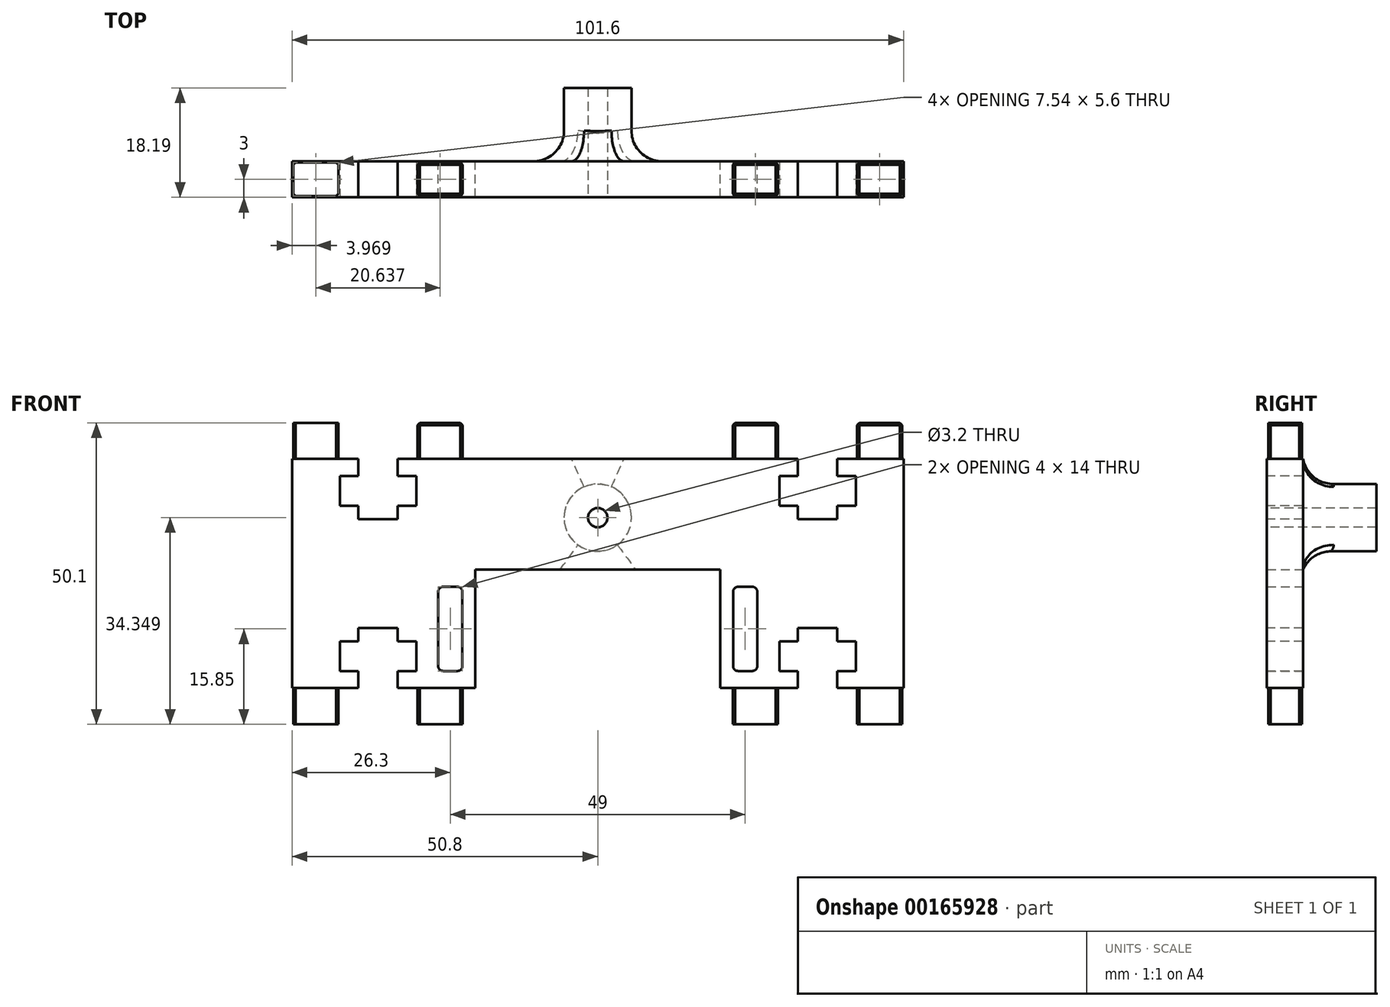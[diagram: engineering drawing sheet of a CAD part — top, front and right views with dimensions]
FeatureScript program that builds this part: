
annotation { "Feature Type Name" : "Feature", "Feature Type Description" : "" }
export const myFeature = defineFeature(function(context is Context, id is Id, definition is map)
    precondition{}
    {
        {
            var Q0;
            Q0=qCreatedBy(makeId("Front.planeOp"),FACE);
            var sketch = newSketch(context, id + "F0", { "sketchPlane" : qUnion([Q0])});
            skLineSegment(sketch, "E0.bottom", {"start": v(-50.8, 38.1) * mm, "end": v(50.8, 38.1) * mm});
            skLineSegment(sketch, "E0.top", {"start": v(-50.8, 0) * mm, "end": v(50.8, 0) * mm});
            skLineSegment(sketch, "E0.left", {"start": v(-50.8, 38.1) * mm, "end": v(-50.8, 0) * mm});
            skLineSegment(sketch, "E0.right", {"start": v(50.8, 38.1) * mm, "end": v(50.8, 0) * mm});
            skPoint(sketch, "E1", {"position": v(0, 0) * mm});
            skLineSegment(sketch, "E2.bottom", {"start": v(-20.35, 0) * mm, "end": v(20.35, 0) * mm});
            skLineSegment(sketch, "E2.top", {"start": v(-20.35, 19.7) * mm, "end": v(20.35, 19.7) * mm});
            skLineSegment(sketch, "E2.left", {"start": v(-20.35, 0) * mm, "end": v(-20.35, 19.7) * mm});
            skLineSegment(sketch, "E2.right", {"start": v(20.35, 0) * mm, "end": v(20.35, 19.7) * mm});
            skPoint(sketch, "E3", {"position": v(0, 19.7) * mm});
            skLineSegment(sketch, "E4.bottom", {"start": v(22.5, 16.85) * mm, "end": v(26.5, 16.85) * mm});
            skLineSegment(sketch, "E4.top", {"start": v(22.5, 2.85) * mm, "end": v(26.5, 2.85) * mm});
            skLineSegment(sketch, "E4.left", {"start": v(22.5, 16.85) * mm, "end": v(22.5, 2.85) * mm});
            skLineSegment(sketch, "E4.right", {"start": v(26.5, 16.85) * mm, "end": v(26.5, 2.85) * mm});
            skLineSegment(sketch, "E5", {"start": v(-20.35, 9.85) * mm, "end": v(36.92, 9.85) * mm, "construction": true});
            skPoint(sketch, "E6", {"position": v(26.5, 9.85) * mm});
            skLineSegment(sketch, "E7", {"start": v(24.5, 16.85) * mm, "end": v(24.5, 2.85) * mm, "construction": true});
            skLineSegment(sketch, "E8.MirrorCS", {"start": v(-22.5, 16.85) * mm, "end": v(-22.5, 2.85) * mm});
            skLineSegment(sketch, "E9.MirrorCS", {"start": v(-26.5, 16.85) * mm, "end": v(-26.5, 2.85) * mm});
            skLineSegment(sketch, "E10.MirrorCS", {"start": v(-22.5, 16.85) * mm, "end": v(-26.5, 16.85) * mm});
            skLineSegment(sketch, "E11.MirrorCS", {"start": v(-22.5, 2.85) * mm, "end": v(-26.5, 2.85) * mm});
            skSolve(sketch);
        }
        {
            var Q0;
            Q0=makeQuery(id+"F0.imprint","IMPRINT",FACE,{"disambiguationData":[TD([[makeQuery(id+"F0.imprint","IMPRINT",EDGE,{"derivedFrom":sQuery(id+"F0.wireOp",EDGE,"E0.bottom")}),-1.0]])]});
            extrude(context, id + "F1", {"entities" : qUnion([Q0]), "depth" : 6 * mm});
        }
        {
            var Q0;
            Q0=makeQuery(id+"F1.opExtrude","SWEPT_EDGE",EDGE,{"disambiguationData":[OSD([sQuery(id+"F0.wireOp",EDGE,"E9.MirrorCS"),sQuery(id+"F0.wireOp",EDGE,"E10.MirrorCS")])]});
            var Q1;
            Q1=makeQuery(id+"F1.opExtrude","SWEPT_EDGE",EDGE,{"disambiguationData":[OSD([sQuery(id+"F0.wireOp",EDGE,"E8.MirrorCS"),sQuery(id+"F0.wireOp",EDGE,"E11.MirrorCS")])]});
            var Q2;
            Q2=makeQuery(id+"F1.opExtrude","SWEPT_EDGE",EDGE,{"disambiguationData":[OSD([sQuery(id+"F0.wireOp",EDGE,"E8.MirrorCS"),sQuery(id+"F0.wireOp",EDGE,"E10.MirrorCS")])]});
            var Q3;
            Q3=makeQuery(id+"F1.opExtrude","SWEPT_EDGE",EDGE,{"disambiguationData":[OSD([sQuery(id+"F0.wireOp",EDGE,"E9.MirrorCS"),sQuery(id+"F0.wireOp",EDGE,"E11.MirrorCS")])]});
            var Q4;
            Q4=makeQuery(id+"F1.opExtrude","SWEPT_EDGE",EDGE,{"disambiguationData":[OSD([sQuery(id+"F0.wireOp",EDGE,"E4.top"),sQuery(id+"F0.wireOp",EDGE,"E4.left")])]});
            var Q5;
            Q5=makeQuery(id+"F1.opExtrude","SWEPT_EDGE",EDGE,{"disambiguationData":[OSD([sQuery(id+"F0.wireOp",EDGE,"E4.bottom"),sQuery(id+"F0.wireOp",EDGE,"E4.left")])]});
            var Q6;
            Q6=makeQuery(id+"F1.opExtrude","SWEPT_EDGE",EDGE,{"disambiguationData":[OSD([sQuery(id+"F0.wireOp",EDGE,"E4.bottom"),sQuery(id+"F0.wireOp",EDGE,"E4.right")])]});
            var Q7;
            Q7=makeQuery(id+"F1.opExtrude","SWEPT_EDGE",EDGE,{"disambiguationData":[OSD([sQuery(id+"F0.wireOp",EDGE,"E4.top"),sQuery(id+"F0.wireOp",EDGE,"E4.right")])]});
            fillet(context, id + "F2", {"entities" : qUnion([Q0, Q1, Q2, Q3, Q4, Q5, Q6, Q7]), "radius" : .8 * mm, "tangentPropagation" : true, "allowEdgeOverflow" : false});
        }
        {
            var Q0;
            {var subQ0=sQuery(id+"F0.wireOp",EDGE,"E0.top");Q0=makeQuery(id+"F1.opExtrude","SWEPT_FACE",FACE,{"disambiguationData":[OSD([subQ0]),TDD([makeQuery(id+"F0.imprint","IMPRINT",EDGE,{"disambiguationData":[TD([[makeQuery(id+"F0.imprint","INTERSECT",VERTEX,{"derivedFrom":[subQ0,sQuery(id+"F0.wireOp",EDGE,"E0.left")]}),-1.0]])],"derivedFrom":subQ0})])]});}
            var sketch = newSketch(context, id + "F3", { "sketchPlane" : qUnion([Q0])});
            skLineSegment(sketch, "E12.bottom", {"start": v(-50.8, 6) * mm, "end": v(-42.86, 6) * mm});
            skLineSegment(sketch, "E12.top", {"start": v(-50.8, 0) * mm, "end": v(-42.86, 0) * mm});
            skLineSegment(sketch, "E12.left", {"start": v(-50.8, 6) * mm, "end": v(-50.8, 0) * mm});
            skLineSegment(sketch, "E12.right", {"start": v(-42.86, 6) * mm, "end": v(-42.86, 0) * mm});
            skLineSegment(sketch, "E13.MirrorCS", {"start": v(50.8, 0) * mm, "end": v(42.86, 0) * mm});
            skLineSegment(sketch, "E14.MirrorCS", {"start": v(42.86, 6) * mm, "end": v(42.86, 0) * mm});
            skLineSegment(sketch, "E15.MirrorCS", {"start": v(50.8, 6) * mm, "end": v(42.86, 6) * mm});
            skLineSegment(sketch, "E16.MirrorCS", {"start": v(50.8, 6) * mm, "end": v(50.8, 0) * mm});
            skLineSegment(sketch, "E17.bottom", {"start": v(-30.16, 6) * mm, "end": v(-22.23, 6) * mm});
            skLineSegment(sketch, "E17.top", {"start": v(-30.16, 0) * mm, "end": v(-22.23, 0) * mm});
            skLineSegment(sketch, "E17.left", {"start": v(-30.16, 6) * mm, "end": v(-30.16, 0) * mm});
            skLineSegment(sketch, "E17.right", {"start": v(-22.23, 6) * mm, "end": v(-22.23, 0) * mm});
            skLineSegment(sketch, "E18.bottom", {"start": v(30.16, 6) * mm, "end": v(22.23, 6) * mm});
            skLineSegment(sketch, "E18.top", {"start": v(30.16, 0) * mm, "end": v(22.23, 0) * mm});
            skLineSegment(sketch, "E18.left", {"start": v(30.16, 6) * mm, "end": v(30.16, 0) * mm});
            skLineSegment(sketch, "E18.right", {"start": v(22.23, 6) * mm, "end": v(22.23, 0) * mm});
            skSolve(sketch);
        }
        {
            var Q0;
            Q0 = qSketchRegion(id + "F3", true);
            extrude(context, id + "F4", {"entities" : qUnion([Q0]), "operationType" : NewBodyOperationType.ADD, "depth" : 6 * mm});
        }
        {
            var Q0;
            Q0=makeQuery(id+"F1.opExtrude","SWEPT_FACE",FACE,{"disambiguationData":[OSD([sQuery(id+"F0.wireOp",EDGE,"E0.bottom")])]});
            var sketch = newSketch(context, id + "F5", { "sketchPlane" : qUnion([Q0])});
            skLineSegment(sketch, "E19.bottom", {"start": v(-50.8, 0) * mm, "end": v(-42.86, 0) * mm});
            skLineSegment(sketch, "E19.top", {"start": v(-50.8, -6) * mm, "end": v(-42.86, -6) * mm});
            skLineSegment(sketch, "E19.left", {"start": v(-50.8, 0) * mm, "end": v(-50.8, -6) * mm});
            skLineSegment(sketch, "E19.right", {"start": v(-42.86, 0) * mm, "end": v(-42.86, -6) * mm});
            skLineSegment(sketch, "E20.bottom", {"start": v(-30.16, 0) * mm, "end": v(-22.22, 0) * mm});
            skLineSegment(sketch, "E20.top", {"start": v(-30.16, -6) * mm, "end": v(-22.22, -6) * mm});
            skLineSegment(sketch, "E20.left", {"start": v(-30.16, 0) * mm, "end": v(-30.16, -6) * mm});
            skLineSegment(sketch, "E20.right", {"start": v(-22.22, 0) * mm, "end": v(-22.22, -6) * mm});
            skLineSegment(sketch, "E21.bottom", {"start": v(22.23, 0) * mm, "end": v(30.16, 0) * mm});
            skLineSegment(sketch, "E21.top", {"start": v(22.23, -6) * mm, "end": v(30.16, -6) * mm});
            skLineSegment(sketch, "E21.left", {"start": v(22.23, 0) * mm, "end": v(22.23, -6) * mm});
            skLineSegment(sketch, "E21.right", {"start": v(30.16, 0) * mm, "end": v(30.16, -6) * mm});
            skLineSegment(sketch, "E22.bottom", {"start": v(42.86, 0) * mm, "end": v(50.8, 0) * mm});
            skLineSegment(sketch, "E22.top", {"start": v(42.86, -6) * mm, "end": v(50.8, -6) * mm});
            skLineSegment(sketch, "E22.left", {"start": v(42.86, 0) * mm, "end": v(42.86, -6) * mm});
            skLineSegment(sketch, "E22.right", {"start": v(50.8, 0) * mm, "end": v(50.8, -6) * mm});
            skSolve(sketch);
        }
        {
            var Q0;
            Q0 = qSketchRegion(id + "F5", true);
            extrude(context, id + "F6", {"entities" : qUnion([Q0]), "operationType" : NewBodyOperationType.ADD, "depth" : 6 * mm});
        }
        {
            var Q0;
            Q0=makeQuery(id+"F6.boolean.opBoolean","MERGE",FACE,{"derivedFrom":[makeQuery(id+"F4.boolean.opBoolean","MERGE",FACE,{"derivedFrom":[makeQuery(id+"F1.opExtrude","CAP_FACE",FACE,{"disambiguationData":[OSD([sQuery(id+"F0.wireOp",EDGE,"E0.bottom"),sQuery(id+"F0.wireOp",EDGE,"E0.top"),sQuery(id+"F0.wireOp",EDGE,"E0.left"),sQuery(id+"F0.wireOp",EDGE,"E0.right"),sQuery(id+"F0.wireOp",EDGE,"E2.top"),sQuery(id+"F0.wireOp",EDGE,"E2.left"),sQuery(id+"F0.wireOp",EDGE,"E2.right"),sQuery(id+"F0.wireOp",EDGE,"E4.bottom"),sQuery(id+"F0.wireOp",EDGE,"E4.top"),sQuery(id+"F0.wireOp",EDGE,"E4.left"),sQuery(id+"F0.wireOp",EDGE,"E4.right"),sQuery(id+"F0.wireOp",EDGE,"E8.MirrorCS"),sQuery(id+"F0.wireOp",EDGE,"E9.MirrorCS"),sQuery(id+"F0.wireOp",EDGE,"E10.MirrorCS"),sQuery(id+"F0.wireOp",EDGE,"E11.MirrorCS")])],"isStart":false}),makeQuery(id+"F4.opExtrude","SWEPT_FACE",FACE,{"disambiguationData":[OSD([sQuery(id+"F3.wireOp",EDGE,"E12.bottom")])]}),makeQuery(id+"F4.opExtrude","SWEPT_FACE",FACE,{"disambiguationData":[OSD([sQuery(id+"F3.wireOp",EDGE,"E15.MirrorCS")])]}),makeQuery(id+"F4.opExtrude","SWEPT_FACE",FACE,{"disambiguationData":[OSD([sQuery(id+"F3.wireOp",EDGE,"E17.bottom")])]}),makeQuery(id+"F4.opExtrude","SWEPT_FACE",FACE,{"disambiguationData":[OSD([sQuery(id+"F3.wireOp",EDGE,"E18.bottom")])]})]}),makeQuery(id+"F6.opExtrude","SWEPT_FACE",FACE,{"disambiguationData":[OSD([sQuery(id+"F5.wireOp",EDGE,"E19.top")])]}),makeQuery(id+"F6.opExtrude","SWEPT_FACE",FACE,{"disambiguationData":[OSD([sQuery(id+"F5.wireOp",EDGE,"E20.top")])]}),makeQuery(id+"F6.opExtrude","SWEPT_FACE",FACE,{"disambiguationData":[OSD([sQuery(id+"F5.wireOp",EDGE,"E21.top")])]}),makeQuery(id+"F6.opExtrude","SWEPT_FACE",FACE,{"disambiguationData":[OSD([sQuery(id+"F5.wireOp",EDGE,"E22.top")])]})]});
            var sketch = newSketch(context, id + "F7", { "sketchPlane" : qUnion([Q0])});
            skLineSegment(sketch, "E23", {"start": v(0, 38.1) * mm, "end": v(0, 19.7) * mm, "construction": true});
            skLineSegment(sketch, "E24", {"start": v(-50.8, 19.05) * mm, "end": v(50.8, 19.05) * mm, "construction": true});
            skLineSegment(sketch, "E25", {"start": v(-36.51, 38.1) * mm, "end": v(-39.76, 38.1) * mm});
            skLineSegment(sketch, "E26", {"start": v(-39.76, 38.1) * mm, "end": v(-39.76, 35.3) * mm});
            skLineSegment(sketch, "E27", {"start": v(-39.76, 35.3) * mm, "end": v(-42.86, 35.3) * mm});
            skLineSegment(sketch, "E28", {"start": v(-42.86, 35.3) * mm, "end": v(-42.86, 30.3) * mm});
            skLineSegment(sketch, "E29", {"start": v(-42.86, 30.3) * mm, "end": v(-39.76, 30.3) * mm});
            skLineSegment(sketch, "E30", {"start": v(-39.76, 30.3) * mm, "end": v(-39.76, 28.1) * mm});
            skLineSegment(sketch, "E31", {"start": v(-39.76, 28.1) * mm, "end": v(-36.51, 28.1) * mm});
            skLineSegment(sketch, "E32", {"start": v(-36.51, 38.1) * mm, "end": v(-36.51, 28.1) * mm, "construction": true});
            skLineSegment(sketch, "E33.MirrorCS", {"start": v(-36.51, 38.1) * mm, "end": v(-33.26, 38.1) * mm});
            skLineSegment(sketch, "E34.MirrorCS", {"start": v(-33.26, 38.1) * mm, "end": v(-33.26, 35.3) * mm});
            skLineSegment(sketch, "E35.MirrorCS", {"start": v(-33.26, 35.3) * mm, "end": v(-30.16, 35.3) * mm});
            skLineSegment(sketch, "E36.MirrorCS", {"start": v(-30.16, 35.3) * mm, "end": v(-30.16, 30.3) * mm});
            skLineSegment(sketch, "E37.MirrorCS", {"start": v(-30.16, 30.3) * mm, "end": v(-33.26, 30.3) * mm});
            skLineSegment(sketch, "E38.MirrorCS", {"start": v(-33.26, 30.3) * mm, "end": v(-33.26, 28.1) * mm});
            skLineSegment(sketch, "E39.MirrorCS", {"start": v(-33.26, 28.1) * mm, "end": v(-36.51, 28.1) * mm});
            skLineSegment(sketch, "E40.MirrorCS", {"start": v(39.76, 38.1) * mm, "end": v(39.76, 35.3) * mm});
            skLineSegment(sketch, "E41.MirrorCS", {"start": v(33.26, 38.1) * mm, "end": v(33.26, 35.3) * mm});
            skLineSegment(sketch, "E42.MirrorCS", {"start": v(33.26, 35.3) * mm, "end": v(30.16, 35.3) * mm});
            skLineSegment(sketch, "E43.MirrorCS", {"start": v(36.51, 38.1) * mm, "end": v(39.76, 38.1) * mm});
            skLineSegment(sketch, "E44.MirrorCS", {"start": v(36.51, 38.1) * mm, "end": v(33.26, 38.1) * mm});
            skLineSegment(sketch, "E45.MirrorCS", {"start": v(30.16, 35.3) * mm, "end": v(30.16, 30.3) * mm});
            skLineSegment(sketch, "E46.MirrorCS", {"start": v(30.16, 30.3) * mm, "end": v(33.26, 30.3) * mm});
            skLineSegment(sketch, "E47.MirrorCS", {"start": v(33.26, 30.3) * mm, "end": v(33.26, 28.1) * mm});
            skLineSegment(sketch, "E48.MirrorCS", {"start": v(33.26, 28.1) * mm, "end": v(36.51, 28.1) * mm});
            skLineSegment(sketch, "E49.MirrorCS", {"start": v(39.76, 28.1) * mm, "end": v(36.51, 28.1) * mm});
            skLineSegment(sketch, "E50.MirrorCS", {"start": v(39.76, 30.3) * mm, "end": v(39.76, 28.1) * mm});
            skLineSegment(sketch, "E51.MirrorCS", {"start": v(42.86, 30.3) * mm, "end": v(39.76, 30.3) * mm});
            skLineSegment(sketch, "E52.MirrorCS", {"start": v(42.86, 35.3) * mm, "end": v(42.86, 30.3) * mm});
            skLineSegment(sketch, "E53.MirrorCS", {"start": v(39.76, 35.3) * mm, "end": v(42.86, 35.3) * mm});
            skLineSegment(sketch, "E54.MirrorCS", {"start": v(33.26, 0) * mm, "end": v(33.26, 2.8) * mm});
            skLineSegment(sketch, "E55.MirrorCS", {"start": v(33.26, 2.8) * mm, "end": v(30.16, 2.8) * mm});
            skLineSegment(sketch, "E56.MirrorCS", {"start": v(30.16, 2.8) * mm, "end": v(30.16, 7.8) * mm});
            skLineSegment(sketch, "E57.MirrorCS", {"start": v(30.16, 7.8) * mm, "end": v(33.26, 7.8) * mm});
            skLineSegment(sketch, "E58.MirrorCS", {"start": v(33.26, 7.8) * mm, "end": v(33.26, 10) * mm});
            skLineSegment(sketch, "E59.MirrorCS", {"start": v(33.26, 10) * mm, "end": v(36.51, 10) * mm});
            skLineSegment(sketch, "E60.MirrorCS", {"start": v(39.76, 10) * mm, "end": v(36.51, 10) * mm});
            skLineSegment(sketch, "E61.MirrorCS", {"start": v(39.76, 7.8) * mm, "end": v(39.76, 10) * mm});
            skLineSegment(sketch, "E62.MirrorCS", {"start": v(42.86, 7.8) * mm, "end": v(39.76, 7.8) * mm});
            skLineSegment(sketch, "E63.MirrorCS", {"start": v(42.86, 2.8) * mm, "end": v(42.86, 7.8) * mm});
            skLineSegment(sketch, "E64.MirrorCS", {"start": v(39.76, 2.8) * mm, "end": v(42.86, 2.8) * mm});
            skLineSegment(sketch, "E65.MirrorCS", {"start": v(39.76, 0) * mm, "end": v(39.76, 2.8) * mm});
            skLineSegment(sketch, "E66.MirrorCS", {"start": v(36.51, 0) * mm, "end": v(39.76, 0) * mm});
            skLineSegment(sketch, "E67.MirrorCS", {"start": v(36.51, 0) * mm, "end": v(33.26, 0) * mm});
            skLineSegment(sketch, "E68.MirrorCS", {"start": v(-39.76, 0) * mm, "end": v(-39.76, 2.8) * mm});
            skLineSegment(sketch, "E69.MirrorCS", {"start": v(-36.51, 0) * mm, "end": v(-39.76, 0) * mm});
            skLineSegment(sketch, "E70.MirrorCS", {"start": v(-36.51, 0) * mm, "end": v(-33.26, 0) * mm});
            skLineSegment(sketch, "E71.MirrorCS", {"start": v(-33.26, 0) * mm, "end": v(-33.26, 2.8) * mm});
            skLineSegment(sketch, "E72.MirrorCS", {"start": v(-33.26, 2.8) * mm, "end": v(-30.16, 2.8) * mm});
            skLineSegment(sketch, "E73.MirrorCS", {"start": v(-30.16, 2.8) * mm, "end": v(-30.16, 7.8) * mm});
            skLineSegment(sketch, "E74.MirrorCS", {"start": v(-30.16, 7.8) * mm, "end": v(-33.26, 7.8) * mm});
            skLineSegment(sketch, "E75.MirrorCS", {"start": v(-33.26, 10) * mm, "end": v(-36.51, 10) * mm});
            skLineSegment(sketch, "E76.MirrorCS", {"start": v(-39.76, 10) * mm, "end": v(-36.51, 10) * mm});
            skLineSegment(sketch, "E77.MirrorCS", {"start": v(-39.76, 7.8) * mm, "end": v(-39.76, 10) * mm});
            skLineSegment(sketch, "E78.MirrorCS", {"start": v(-42.86, 7.8) * mm, "end": v(-39.76, 7.8) * mm});
            skLineSegment(sketch, "E79.MirrorCS", {"start": v(-42.86, 2.8) * mm, "end": v(-42.86, 7.8) * mm});
            skLineSegment(sketch, "E80.MirrorCS", {"start": v(-39.76, 2.8) * mm, "end": v(-42.86, 2.8) * mm});
            skLineSegment(sketch, "E81.MirrorCS", {"start": v(-33.26, 7.8) * mm, "end": v(-33.26, 10) * mm});
            skSolve(sketch);
        }
        {
            var Q0;
            Q0 = qSketchRegion(id + "F7", true);
            extrude(context, id + "F8", {"entities" : qUnion([Q0]), "operationType" : NewBodyOperationType.REMOVE, "oppositeDirection" : true, "depth" : 25.4 * mm});
        }
        {
            var Q0;
            Q0=makeQuery(id+"F4.opExtrude","CAP_FACE",FACE,{"disambiguationData":[OSD([sQuery(id+"F3.wireOp",EDGE,"E12.bottom"),sQuery(id+"F3.wireOp",EDGE,"E12.top"),sQuery(id+"F3.wireOp",EDGE,"E12.left"),sQuery(id+"F3.wireOp",EDGE,"E12.right")])],"isStart":false});
            var sketch = newSketch(context, id + "F9", { "sketchPlane" : qUnion([Q0])});
            skLineSegment(sketch, "E82.bottom", {"start": v(-50.6, 5.8) * mm, "end": v(-43.06, 5.8) * mm});
            skLineSegment(sketch, "E82.top", {"start": v(-50.6, 0.2) * mm, "end": v(-43.06, 0.2) * mm});
            skLineSegment(sketch, "E82.left", {"start": v(-50.6, 5.8) * mm, "end": v(-50.6, 0.2) * mm});
            skLineSegment(sketch, "E82.right", {"start": v(-43.06, 5.8) * mm, "end": v(-43.06, 0.2) * mm});
            skLineSegment(sketch, "E83.bottom", {"start": v(-50.8, 6) * mm, "end": v(-42.86, 6) * mm});
            skLineSegment(sketch, "E83.top", {"start": v(-50.8, 0) * mm, "end": v(-42.86, 0) * mm});
            skLineSegment(sketch, "E83.left", {"start": v(-50.8, 6) * mm, "end": v(-50.8, 0) * mm});
            skLineSegment(sketch, "E83.right", {"start": v(-42.86, 6) * mm, "end": v(-42.86, 0) * mm});
            skLineSegment(sketch, "E84.bottom", {"start": v(-30.16, 6) * mm, "end": v(-22.23, 6) * mm});
            skLineSegment(sketch, "E84.top", {"start": v(-30.16, 0) * mm, "end": v(-22.23, 0) * mm});
            skLineSegment(sketch, "E84.left", {"start": v(-30.16, 6) * mm, "end": v(-30.16, 0) * mm});
            skLineSegment(sketch, "E84.right", {"start": v(-22.23, 6) * mm, "end": v(-22.23, 0) * mm});
            skLineSegment(sketch, "E85.bottom", {"start": v(-29.96, 5.8) * mm, "end": v(-22.43, 5.8) * mm});
            skLineSegment(sketch, "E85.top", {"start": v(-29.96, 0.2) * mm, "end": v(-22.43, 0.2) * mm});
            skLineSegment(sketch, "E85.left", {"start": v(-29.96, 5.8) * mm, "end": v(-29.96, 0.2) * mm});
            skLineSegment(sketch, "E85.right", {"start": v(-22.43, 5.8) * mm, "end": v(-22.43, 0.2) * mm});
            skLineSegment(sketch, "E86", {"start": v(0, 7.46) * mm, "end": v(0, -0.5) * mm, "construction": true});
            skLineSegment(sketch, "E87.MirrorCS", {"start": v(22.23, 6) * mm, "end": v(22.23, 0) * mm});
            skLineSegment(sketch, "E88.MirrorCS", {"start": v(30.16, 0) * mm, "end": v(22.23, 0) * mm});
            skLineSegment(sketch, "E89.MirrorCS", {"start": v(30.16, 6) * mm, "end": v(30.16, 0) * mm});
            skLineSegment(sketch, "E90.MirrorCS", {"start": v(30.16, 6) * mm, "end": v(22.23, 6) * mm});
            skLineSegment(sketch, "E91.MirrorCS", {"start": v(29.96, 5.8) * mm, "end": v(22.43, 5.8) * mm});
            skLineSegment(sketch, "E92.MirrorCS", {"start": v(22.43, 5.8) * mm, "end": v(22.43, 0.2) * mm});
            skLineSegment(sketch, "E93.MirrorCS", {"start": v(29.96, 0.2) * mm, "end": v(22.43, 0.2) * mm});
            skLineSegment(sketch, "E94.MirrorCS", {"start": v(29.96, 5.8) * mm, "end": v(29.96, 0.2) * mm});
            skLineSegment(sketch, "E95.MirrorCS", {"start": v(50.6, 5.8) * mm, "end": v(50.6, 0.2) * mm});
            skLineSegment(sketch, "E96.MirrorCS", {"start": v(50.8, 6) * mm, "end": v(50.8, 0) * mm});
            skLineSegment(sketch, "E97.MirrorCS", {"start": v(50.8, 6) * mm, "end": v(42.86, 6) * mm});
            skLineSegment(sketch, "E98.MirrorCS", {"start": v(42.86, 6) * mm, "end": v(42.86, 0) * mm});
            skLineSegment(sketch, "E99.MirrorCS", {"start": v(50.8, 0) * mm, "end": v(42.86, 0) * mm});
            skLineSegment(sketch, "E100.MirrorCS", {"start": v(50.6, 0.2) * mm, "end": v(43.06, 0.2) * mm});
            skLineSegment(sketch, "E101.MirrorCS", {"start": v(43.06, 5.8) * mm, "end": v(43.06, 0.2) * mm});
            skLineSegment(sketch, "E102.MirrorCS", {"start": v(50.6, 5.8) * mm, "end": v(43.06, 5.8) * mm});
            skSolve(sketch);
        }
        {
            var Q0;
            Q0 = qSketchRegion(id + "F9", true);
            extrude(context, id + "F10", {"entities" : qUnion([Q0]), "operationType" : NewBodyOperationType.REMOVE, "oppositeDirection" : true, "depth" : 6 * mm});
        }
        {
            var Q0;
            Q0=makeQuery(id+"F10.boolean.opBoolean","COPY",EDGE,{"derivedFrom":makeQuery(id+"F10.opExtrude","SWEPT_EDGE",EDGE,{"disambiguationData":[OSD([sQuery(id+"F9.wireOp",EDGE,"E82.bottom"),sQuery(id+"F9.wireOp",EDGE,"E82.left")])]})});
            var Q1;
            Q1=makeQuery(id+"F10.boolean.opBoolean","COPY",EDGE,{"derivedFrom":makeQuery(id+"F10.opExtrude","SWEPT_EDGE",EDGE,{"disambiguationData":[OSD([sQuery(id+"F9.wireOp",EDGE,"E82.bottom"),sQuery(id+"F9.wireOp",EDGE,"E82.right")])]})});
            var Q2;
            Q2=makeQuery(id+"F10.boolean.opBoolean","COPY",EDGE,{"derivedFrom":makeQuery(id+"F10.opExtrude","CAP_EDGE",EDGE,{"disambiguationData":[OSD([sQuery(id+"F9.wireOp",EDGE,"E82.bottom")])],"isStart":true})});
            var Q3;
            Q3=makeQuery(id+"F10.boolean.opBoolean","COPY",EDGE,{"derivedFrom":makeQuery(id+"F10.opExtrude","CAP_EDGE",EDGE,{"disambiguationData":[OSD([sQuery(id+"F9.wireOp",EDGE,"E82.right")])],"isStart":true})});
            var Q4;
            Q4=makeQuery(id+"F10.boolean.opBoolean","COPY",EDGE,{"derivedFrom":makeQuery(id+"F10.opExtrude","CAP_EDGE",EDGE,{"disambiguationData":[OSD([sQuery(id+"F9.wireOp",EDGE,"E82.top")])],"isStart":true})});
            var Q5;
            Q5=makeQuery(id+"F10.boolean.opBoolean","COPY",EDGE,{"derivedFrom":makeQuery(id+"F10.opExtrude","CAP_EDGE",EDGE,{"disambiguationData":[OSD([sQuery(id+"F9.wireOp",EDGE,"E82.left")])],"isStart":true})});
            var Q6;
            Q6=makeQuery(id+"F10.boolean.opBoolean","COPY",EDGE,{"derivedFrom":makeQuery(id+"F10.opExtrude","SWEPT_EDGE",EDGE,{"disambiguationData":[OSD([sQuery(id+"F9.wireOp",EDGE,"E82.top"),sQuery(id+"F9.wireOp",EDGE,"E82.left")])]})});
            var Q7;
            Q7=makeQuery(id+"F10.boolean.opBoolean","COPY",EDGE,{"derivedFrom":makeQuery(id+"F10.opExtrude","SWEPT_EDGE",EDGE,{"disambiguationData":[OSD([sQuery(id+"F9.wireOp",EDGE,"E82.top"),sQuery(id+"F9.wireOp",EDGE,"E82.right")])]})});
            var Q8;
            Q8=makeQuery(id+"F10.boolean.opBoolean","COPY",EDGE,{"derivedFrom":makeQuery(id+"F10.opExtrude","SWEPT_EDGE",EDGE,{"disambiguationData":[OSD([sQuery(id+"F9.wireOp",EDGE,"E85.top"),sQuery(id+"F9.wireOp",EDGE,"E85.left")])]})});
            var Q9;
            Q9=makeQuery(id+"F10.boolean.opBoolean","COPY",EDGE,{"derivedFrom":makeQuery(id+"F10.opExtrude","SWEPT_EDGE",EDGE,{"disambiguationData":[OSD([sQuery(id+"F9.wireOp",EDGE,"E85.bottom"),sQuery(id+"F9.wireOp",EDGE,"E85.left")])]})});
            var Q10;
            Q10=makeQuery(id+"F10.boolean.opBoolean","COPY",EDGE,{"derivedFrom":makeQuery(id+"F10.opExtrude","SWEPT_EDGE",EDGE,{"disambiguationData":[OSD([sQuery(id+"F9.wireOp",EDGE,"E85.top"),sQuery(id+"F9.wireOp",EDGE,"E85.right")])]})});
            var Q11;
            Q11=makeQuery(id+"F10.boolean.opBoolean","COPY",EDGE,{"derivedFrom":makeQuery(id+"F10.opExtrude","CAP_EDGE",EDGE,{"disambiguationData":[OSD([sQuery(id+"F9.wireOp",EDGE,"E85.top")])],"isStart":true})});
            var Q12;
            Q12=makeQuery(id+"F10.boolean.opBoolean","COPY",EDGE,{"derivedFrom":makeQuery(id+"F10.opExtrude","CAP_EDGE",EDGE,{"disambiguationData":[OSD([sQuery(id+"F9.wireOp",EDGE,"E85.left")])],"isStart":true})});
            var Q13;
            Q13=makeQuery(id+"F10.boolean.opBoolean","COPY",EDGE,{"derivedFrom":makeQuery(id+"F10.opExtrude","CAP_EDGE",EDGE,{"disambiguationData":[OSD([sQuery(id+"F9.wireOp",EDGE,"E85.bottom")])],"isStart":true})});
            var Q14;
            Q14=makeQuery(id+"F10.boolean.opBoolean","COPY",EDGE,{"derivedFrom":makeQuery(id+"F10.opExtrude","CAP_EDGE",EDGE,{"disambiguationData":[OSD([sQuery(id+"F9.wireOp",EDGE,"E85.right")])],"isStart":true})});
            var Q15;
            Q15=makeQuery(id+"F10.boolean.opBoolean","COPY",EDGE,{"derivedFrom":makeQuery(id+"F10.opExtrude","SWEPT_EDGE",EDGE,{"disambiguationData":[OSD([sQuery(id+"F9.wireOp",EDGE,"E85.bottom"),sQuery(id+"F9.wireOp",EDGE,"E85.right")])]})});
            var Q16;
            Q16=makeQuery(id+"F10.boolean.opBoolean","COPY",EDGE,{"derivedFrom":makeQuery(id+"F10.opExtrude","SWEPT_EDGE",EDGE,{"disambiguationData":[OSD([sQuery(id+"F9.wireOp",EDGE,"E91.MirrorCS"),sQuery(id+"F9.wireOp",EDGE,"E92.MirrorCS")])]})});
            var Q17;
            Q17=makeQuery(id+"F10.boolean.opBoolean","COPY",EDGE,{"derivedFrom":makeQuery(id+"F10.opExtrude","SWEPT_EDGE",EDGE,{"disambiguationData":[OSD([sQuery(id+"F9.wireOp",EDGE,"E91.MirrorCS"),sQuery(id+"F9.wireOp",EDGE,"E94.MirrorCS")])]})});
            var Q18;
            Q18=makeQuery(id+"F10.boolean.opBoolean","COPY",EDGE,{"derivedFrom":makeQuery(id+"F10.opExtrude","CAP_EDGE",EDGE,{"disambiguationData":[OSD([sQuery(id+"F9.wireOp",EDGE,"E91.MirrorCS")])],"isStart":true})});
            var Q19;
            Q19=makeQuery(id+"F10.boolean.opBoolean","COPY",EDGE,{"derivedFrom":makeQuery(id+"F10.opExtrude","CAP_EDGE",EDGE,{"disambiguationData":[OSD([sQuery(id+"F9.wireOp",EDGE,"E94.MirrorCS")])],"isStart":true})});
            var Q20;
            Q20=makeQuery(id+"F10.boolean.opBoolean","COPY",EDGE,{"derivedFrom":makeQuery(id+"F10.opExtrude","CAP_EDGE",EDGE,{"disambiguationData":[OSD([sQuery(id+"F9.wireOp",EDGE,"E93.MirrorCS")])],"isStart":true})});
            var Q21;
            Q21=makeQuery(id+"F10.boolean.opBoolean","COPY",EDGE,{"derivedFrom":makeQuery(id+"F10.opExtrude","CAP_EDGE",EDGE,{"disambiguationData":[OSD([sQuery(id+"F9.wireOp",EDGE,"E92.MirrorCS")])],"isStart":true})});
            var Q22;
            Q22=makeQuery(id+"F10.boolean.opBoolean","COPY",EDGE,{"derivedFrom":makeQuery(id+"F10.opExtrude","SWEPT_EDGE",EDGE,{"disambiguationData":[OSD([sQuery(id+"F9.wireOp",EDGE,"E92.MirrorCS"),sQuery(id+"F9.wireOp",EDGE,"E93.MirrorCS")])]})});
            var Q23;
            Q23=makeQuery(id+"F10.boolean.opBoolean","COPY",EDGE,{"derivedFrom":makeQuery(id+"F10.opExtrude","SWEPT_EDGE",EDGE,{"disambiguationData":[OSD([sQuery(id+"F9.wireOp",EDGE,"E93.MirrorCS"),sQuery(id+"F9.wireOp",EDGE,"E94.MirrorCS")])]})});
            var Q24;
            Q24=makeQuery(id+"F10.boolean.opBoolean","COPY",EDGE,{"derivedFrom":makeQuery(id+"F10.opExtrude","SWEPT_EDGE",EDGE,{"disambiguationData":[OSD([sQuery(id+"F9.wireOp",EDGE,"E100.MirrorCS"),sQuery(id+"F9.wireOp",EDGE,"E101.MirrorCS")])]})});
            var Q25;
            Q25=makeQuery(id+"F10.boolean.opBoolean","COPY",EDGE,{"derivedFrom":makeQuery(id+"F10.opExtrude","SWEPT_EDGE",EDGE,{"disambiguationData":[OSD([sQuery(id+"F9.wireOp",EDGE,"E101.MirrorCS"),sQuery(id+"F9.wireOp",EDGE,"E102.MirrorCS")])]})});
            var Q26;
            Q26=makeQuery(id+"F10.boolean.opBoolean","COPY",EDGE,{"derivedFrom":makeQuery(id+"F10.opExtrude","SWEPT_EDGE",EDGE,{"disambiguationData":[OSD([sQuery(id+"F9.wireOp",EDGE,"E95.MirrorCS"),sQuery(id+"F9.wireOp",EDGE,"E100.MirrorCS")])]})});
            var Q27;
            Q27=makeQuery(id+"F10.boolean.opBoolean","COPY",EDGE,{"derivedFrom":makeQuery(id+"F10.opExtrude","CAP_EDGE",EDGE,{"disambiguationData":[OSD([sQuery(id+"F9.wireOp",EDGE,"E100.MirrorCS")])],"isStart":true})});
            var Q28;
            Q28=makeQuery(id+"F10.boolean.opBoolean","COPY",EDGE,{"derivedFrom":makeQuery(id+"F10.opExtrude","CAP_EDGE",EDGE,{"disambiguationData":[OSD([sQuery(id+"F9.wireOp",EDGE,"E101.MirrorCS")])],"isStart":true})});
            var Q29;
            Q29=makeQuery(id+"F10.boolean.opBoolean","COPY",EDGE,{"derivedFrom":makeQuery(id+"F10.opExtrude","CAP_EDGE",EDGE,{"disambiguationData":[OSD([sQuery(id+"F9.wireOp",EDGE,"E102.MirrorCS")])],"isStart":true})});
            var Q30;
            Q30=makeQuery(id+"F10.boolean.opBoolean","COPY",EDGE,{"derivedFrom":makeQuery(id+"F10.opExtrude","CAP_EDGE",EDGE,{"disambiguationData":[OSD([sQuery(id+"F9.wireOp",EDGE,"E95.MirrorCS")])],"isStart":true})});
            var Q31;
            Q31=makeQuery(id+"F10.boolean.opBoolean","COPY",EDGE,{"derivedFrom":makeQuery(id+"F10.opExtrude","SWEPT_EDGE",EDGE,{"disambiguationData":[OSD([sQuery(id+"F9.wireOp",EDGE,"E95.MirrorCS"),sQuery(id+"F9.wireOp",EDGE,"E102.MirrorCS")])]})});
            chamfer(context, id + "F11", {"entities" : qUnion([Q0, Q1, Q2, Q3, Q4, Q5, Q6, Q7, Q8, Q9, Q10, Q11, Q12, Q13, Q14, Q15, Q16, Q17, Q18, Q19, Q20, Q21, Q22, Q23, Q24, Q25, Q26, Q27, Q28, Q29, Q30, Q31]), "width" : .4 * mm, "tangentPropagation" : true});
        }
        {
            var Q0;
            Q0=makeQuery(id+"F6.opExtrude","CAP_FACE",FACE,{"disambiguationData":[OSD([sQuery(id+"F5.wireOp",EDGE,"E19.bottom"),sQuery(id+"F5.wireOp",EDGE,"E19.top"),sQuery(id+"F5.wireOp",EDGE,"E19.left"),sQuery(id+"F5.wireOp",EDGE,"E19.right")])],"isStart":false});
            var sketch = newSketch(context, id + "F12", { "sketchPlane" : qUnion([Q0])});
            skLineSegment(sketch, "E103.bottom", {"start": v(-50.6, -0.2) * mm, "end": v(-43.06, -0.2) * mm});
            skLineSegment(sketch, "E103.top", {"start": v(-50.6, -5.8) * mm, "end": v(-43.06, -5.8) * mm});
            skLineSegment(sketch, "E103.left", {"start": v(-50.6, -0.2) * mm, "end": v(-50.6, -5.8) * mm});
            skLineSegment(sketch, "E103.right", {"start": v(-43.06, -0.2) * mm, "end": v(-43.06, -5.8) * mm});
            skLineSegment(sketch, "E104.bottom", {"start": v(-50.8, 0) * mm, "end": v(-42.86, 0) * mm});
            skLineSegment(sketch, "E104.top", {"start": v(-50.8, -6) * mm, "end": v(-42.86, -6) * mm});
            skLineSegment(sketch, "E104.left", {"start": v(-50.8, 0) * mm, "end": v(-50.8, -6) * mm});
            skLineSegment(sketch, "E104.right", {"start": v(-42.86, 0) * mm, "end": v(-42.86, -6) * mm});
            skLineSegment(sketch, "E105.bottom", {"start": v(-30.16, 0) * mm, "end": v(-22.22, 0) * mm});
            skLineSegment(sketch, "E105.top", {"start": v(-30.16, -6) * mm, "end": v(-22.22, -6) * mm});
            skLineSegment(sketch, "E105.left", {"start": v(-30.16, 0) * mm, "end": v(-30.16, -6) * mm});
            skLineSegment(sketch, "E105.right", {"start": v(-22.22, 0) * mm, "end": v(-22.22, -6) * mm});
            skLineSegment(sketch, "E106.bottom", {"start": v(-29.96, -0.2) * mm, "end": v(-22.43, -0.2) * mm});
            skLineSegment(sketch, "E106.top", {"start": v(-29.96, -5.8) * mm, "end": v(-22.42, -5.8) * mm});
            skLineSegment(sketch, "E106.left", {"start": v(-29.96, -0.2) * mm, "end": v(-29.96, -5.8) * mm});
            skLineSegment(sketch, "E106.right", {"start": v(-22.42, -0.2) * mm, "end": v(-22.42, -5.8) * mm});
            skLineSegment(sketch, "E107", {"start": v(0, -2.64) * mm, "end": v(0, -10.6) * mm, "construction": true});
            skLineSegment(sketch, "E108.MirrorCS", {"start": v(22.22, 0) * mm, "end": v(22.22, -6) * mm});
            skLineSegment(sketch, "E109.MirrorCS", {"start": v(30.16, -6) * mm, "end": v(22.22, -6) * mm});
            skLineSegment(sketch, "E110.MirrorCS", {"start": v(30.16, 0) * mm, "end": v(30.16, -6) * mm});
            skLineSegment(sketch, "E111.MirrorCS", {"start": v(30.16, 0) * mm, "end": v(22.22, 0) * mm});
            skLineSegment(sketch, "E112.MirrorCS", {"start": v(29.96, -0.2) * mm, "end": v(22.42, -0.2) * mm});
            skLineSegment(sketch, "E113.MirrorCS", {"start": v(22.42, -0.2) * mm, "end": v(22.42, -5.8) * mm});
            skLineSegment(sketch, "E114.MirrorCS", {"start": v(29.96, -5.8) * mm, "end": v(22.42, -5.8) * mm});
            skLineSegment(sketch, "E115.MirrorCS", {"start": v(29.96, -0.2) * mm, "end": v(29.96, -5.8) * mm});
            skLineSegment(sketch, "E116.MirrorCS", {"start": v(50.6, -0.2) * mm, "end": v(50.6, -5.8) * mm});
            skLineSegment(sketch, "E117.MirrorCS", {"start": v(50.8, 0) * mm, "end": v(50.8, -6) * mm});
            skLineSegment(sketch, "E118.MirrorCS", {"start": v(50.8, 0) * mm, "end": v(42.86, 0) * mm});
            skLineSegment(sketch, "E119.MirrorCS", {"start": v(42.86, 0) * mm, "end": v(42.86, -6) * mm});
            skLineSegment(sketch, "E120.MirrorCS", {"start": v(50.8, -6) * mm, "end": v(42.86, -6) * mm});
            skLineSegment(sketch, "E121.MirrorCS", {"start": v(50.6, -5.8) * mm, "end": v(43.06, -5.8) * mm});
            skLineSegment(sketch, "E122.MirrorCS", {"start": v(43.06, -0.2) * mm, "end": v(43.06, -5.8) * mm});
            skLineSegment(sketch, "E123.MirrorCS", {"start": v(50.6, -0.2) * mm, "end": v(43.06, -0.2) * mm});
            skSolve(sketch);
        }
        {
            var Q0;
            Q0 = qSketchRegion(id + "F12", true);
            extrude(context, id + "F13", {"entities" : qUnion([Q0]), "operationType" : NewBodyOperationType.REMOVE, "oppositeDirection" : true, "depth" : 6 * mm});
        }
        {
            var Q0;
            Q0=makeQuery(id+"F13.boolean.opBoolean","COPY",EDGE,{"derivedFrom":makeQuery(id+"F13.opExtrude","SWEPT_EDGE",EDGE,{"disambiguationData":[OSD([sQuery(id+"F12.wireOp",EDGE,"E103.bottom"),sQuery(id+"F12.wireOp",EDGE,"E103.left")])]})});
            var Q1;
            Q1=makeQuery(id+"F13.boolean.opBoolean","COPY",EDGE,{"derivedFrom":makeQuery(id+"F13.opExtrude","CAP_EDGE",EDGE,{"disambiguationData":[OSD([sQuery(id+"F12.wireOp",EDGE,"E103.left")])],"isStart":true})});
            var Q2;
            Q2=makeQuery(id+"F13.boolean.opBoolean","COPY",EDGE,{"derivedFrom":makeQuery(id+"F13.opExtrude","SWEPT_EDGE",EDGE,{"disambiguationData":[OSD([sQuery(id+"F12.wireOp",EDGE,"E103.top"),sQuery(id+"F12.wireOp",EDGE,"E103.left")])]})});
            var Q3;
            Q3=makeQuery(id+"F13.boolean.opBoolean","COPY",EDGE,{"derivedFrom":makeQuery(id+"F13.opExtrude","CAP_EDGE",EDGE,{"disambiguationData":[OSD([sQuery(id+"F12.wireOp",EDGE,"E103.top")])],"isStart":true})});
            var Q4;
            Q4=makeQuery(id+"F13.boolean.opBoolean","COPY",EDGE,{"derivedFrom":makeQuery(id+"F13.opExtrude","CAP_EDGE",EDGE,{"disambiguationData":[OSD([sQuery(id+"F12.wireOp",EDGE,"E103.bottom")])],"isStart":true})});
            var Q5;
            Q5=makeQuery(id+"F13.boolean.opBoolean","COPY",EDGE,{"derivedFrom":makeQuery(id+"F13.opExtrude","CAP_EDGE",EDGE,{"disambiguationData":[OSD([sQuery(id+"F12.wireOp",EDGE,"E103.right")])],"isStart":true})});
            var Q6;
            Q6=makeQuery(id+"F13.boolean.opBoolean","COPY",EDGE,{"derivedFrom":makeQuery(id+"F13.opExtrude","SWEPT_EDGE",EDGE,{"disambiguationData":[OSD([sQuery(id+"F12.wireOp",EDGE,"E103.bottom"),sQuery(id+"F12.wireOp",EDGE,"E103.right")])]})});
            var Q7;
            Q7=makeQuery(id+"F13.boolean.opBoolean","COPY",EDGE,{"derivedFrom":makeQuery(id+"F13.opExtrude","SWEPT_EDGE",EDGE,{"disambiguationData":[OSD([sQuery(id+"F12.wireOp",EDGE,"E103.top"),sQuery(id+"F12.wireOp",EDGE,"E103.right")])]})});
            var Q8;
            Q8=makeQuery(id+"F13.boolean.opBoolean","COPY",EDGE,{"derivedFrom":makeQuery(id+"F13.opExtrude","SWEPT_EDGE",EDGE,{"disambiguationData":[OSD([sQuery(id+"F12.wireOp",EDGE,"E106.bottom"),sQuery(id+"F12.wireOp",EDGE,"E106.left")])]})});
            var Q9;
            Q9=makeQuery(id+"F6.opExtrude","CAP_FACE",FACE,{"disambiguationData":[OSD([sQuery(id+"F5.wireOp",EDGE,"E20.bottom"),sQuery(id+"F5.wireOp",EDGE,"E20.top"),sQuery(id+"F5.wireOp",EDGE,"E20.left"),sQuery(id+"F5.wireOp",EDGE,"E20.right")])],"isStart":false});
            var Q10;
            Q10=makeQuery(id+"F13.boolean.opBoolean","COPY",EDGE,{"derivedFrom":makeQuery(id+"F13.opExtrude","SWEPT_EDGE",EDGE,{"disambiguationData":[OSD([sQuery(id+"F12.wireOp",EDGE,"E106.bottom"),sQuery(id+"F12.wireOp",EDGE,"E106.right")])]})});
            var Q11;
            Q11=makeQuery(id+"F13.boolean.opBoolean","COPY",EDGE,{"derivedFrom":makeQuery(id+"F13.opExtrude","SWEPT_EDGE",EDGE,{"disambiguationData":[OSD([sQuery(id+"F12.wireOp",EDGE,"E106.top"),sQuery(id+"F12.wireOp",EDGE,"E106.left")])]})});
            var Q12;
            Q12=makeQuery(id+"F13.boolean.opBoolean","COPY",EDGE,{"derivedFrom":makeQuery(id+"F13.opExtrude","SWEPT_EDGE",EDGE,{"disambiguationData":[OSD([sQuery(id+"F12.wireOp",EDGE,"E106.top"),sQuery(id+"F12.wireOp",EDGE,"E106.right")])]})});
            var Q13;
            Q13=makeQuery(id+"F6.opExtrude","CAP_FACE",FACE,{"disambiguationData":[OSD([sQuery(id+"F5.wireOp",EDGE,"E21.bottom"),sQuery(id+"F5.wireOp",EDGE,"E21.top"),sQuery(id+"F5.wireOp",EDGE,"E21.left"),sQuery(id+"F5.wireOp",EDGE,"E21.right")])],"isStart":false});
            var Q14;
            Q14=makeQuery(id+"F6.opExtrude","CAP_FACE",FACE,{"disambiguationData":[OSD([sQuery(id+"F5.wireOp",EDGE,"E22.bottom"),sQuery(id+"F5.wireOp",EDGE,"E22.top"),sQuery(id+"F5.wireOp",EDGE,"E22.left"),sQuery(id+"F5.wireOp",EDGE,"E22.right")])],"isStart":false});
            var Q15;
            Q15=makeQuery(id+"F13.boolean.opBoolean","COPY",EDGE,{"derivedFrom":makeQuery(id+"F13.opExtrude","SWEPT_EDGE",EDGE,{"disambiguationData":[OSD([sQuery(id+"F12.wireOp",EDGE,"E116.MirrorCS"),sQuery(id+"F12.wireOp",EDGE,"E121.MirrorCS")])]})});
            var Q16;
            Q16=makeQuery(id+"F13.boolean.opBoolean","COPY",EDGE,{"derivedFrom":makeQuery(id+"F13.opExtrude","SWEPT_EDGE",EDGE,{"disambiguationData":[OSD([sQuery(id+"F12.wireOp",EDGE,"E116.MirrorCS"),sQuery(id+"F12.wireOp",EDGE,"E123.MirrorCS")])]})});
            var Q17;
            Q17=makeQuery(id+"F13.boolean.opBoolean","COPY",EDGE,{"derivedFrom":makeQuery(id+"F13.opExtrude","SWEPT_EDGE",EDGE,{"disambiguationData":[OSD([sQuery(id+"F12.wireOp",EDGE,"E121.MirrorCS"),sQuery(id+"F12.wireOp",EDGE,"E122.MirrorCS")])]})});
            var Q18;
            Q18=makeQuery(id+"F13.boolean.opBoolean","COPY",EDGE,{"derivedFrom":makeQuery(id+"F13.opExtrude","SWEPT_EDGE",EDGE,{"disambiguationData":[OSD([sQuery(id+"F12.wireOp",EDGE,"E122.MirrorCS"),sQuery(id+"F12.wireOp",EDGE,"E123.MirrorCS")])]})});
            var Q19;
            Q19=makeQuery(id+"F13.boolean.opBoolean","COPY",EDGE,{"derivedFrom":makeQuery(id+"F13.opExtrude","SWEPT_EDGE",EDGE,{"disambiguationData":[OSD([sQuery(id+"F12.wireOp",EDGE,"E112.MirrorCS"),sQuery(id+"F12.wireOp",EDGE,"E115.MirrorCS")])]})});
            var Q20;
            Q20=makeQuery(id+"F13.boolean.opBoolean","COPY",EDGE,{"derivedFrom":makeQuery(id+"F13.opExtrude","SWEPT_EDGE",EDGE,{"disambiguationData":[OSD([sQuery(id+"F12.wireOp",EDGE,"E112.MirrorCS"),sQuery(id+"F12.wireOp",EDGE,"E113.MirrorCS")])]})});
            var Q21;
            Q21=makeQuery(id+"F13.boolean.opBoolean","COPY",EDGE,{"derivedFrom":makeQuery(id+"F13.opExtrude","SWEPT_EDGE",EDGE,{"disambiguationData":[OSD([sQuery(id+"F12.wireOp",EDGE,"E113.MirrorCS"),sQuery(id+"F12.wireOp",EDGE,"E114.MirrorCS")])]})});
            var Q22;
            Q22=makeQuery(id+"F13.boolean.opBoolean","COPY",EDGE,{"derivedFrom":makeQuery(id+"F13.opExtrude","SWEPT_EDGE",EDGE,{"disambiguationData":[OSD([sQuery(id+"F12.wireOp",EDGE,"E114.MirrorCS"),sQuery(id+"F12.wireOp",EDGE,"E115.MirrorCS")])]})});
            chamfer(context, id + "F14", {"entities" : qUnion([Q0, Q1, Q2, Q3, Q4, Q5, Q6, Q7, Q8, Q9, Q10, Q11, Q12, Q13, Q14, Q15, Q16, Q17, Q18, Q19, Q20, Q21, Q22]), "width" : .4 * mm, "tangentPropagation" : true});
        }
        {
            var Q0;
            Q0=makeQuery(id+"F6.boolean.opBoolean","MERGE",FACE,{"derivedFrom":[makeQuery(id+"F4.boolean.opBoolean","MERGE",FACE,{"derivedFrom":[makeQuery(id+"F1.opExtrude","CAP_FACE",FACE,{"disambiguationData":[OSD([sQuery(id+"F0.wireOp",EDGE,"E0.bottom"),sQuery(id+"F0.wireOp",EDGE,"E0.top"),sQuery(id+"F0.wireOp",EDGE,"E0.left"),sQuery(id+"F0.wireOp",EDGE,"E0.right"),sQuery(id+"F0.wireOp",EDGE,"E2.top"),sQuery(id+"F0.wireOp",EDGE,"E2.left"),sQuery(id+"F0.wireOp",EDGE,"E2.right"),sQuery(id+"F0.wireOp",EDGE,"E4.bottom"),sQuery(id+"F0.wireOp",EDGE,"E4.top"),sQuery(id+"F0.wireOp",EDGE,"E4.left"),sQuery(id+"F0.wireOp",EDGE,"E4.right"),sQuery(id+"F0.wireOp",EDGE,"E8.MirrorCS"),sQuery(id+"F0.wireOp",EDGE,"E9.MirrorCS"),sQuery(id+"F0.wireOp",EDGE,"E10.MirrorCS"),sQuery(id+"F0.wireOp",EDGE,"E11.MirrorCS")])],"isStart":false}),makeQuery(id+"F4.opExtrude","SWEPT_FACE",FACE,{"disambiguationData":[OSD([sQuery(id+"F3.wireOp",EDGE,"E12.bottom")])]}),makeQuery(id+"F4.opExtrude","SWEPT_FACE",FACE,{"disambiguationData":[OSD([sQuery(id+"F3.wireOp",EDGE,"E15.MirrorCS")])]}),makeQuery(id+"F4.opExtrude","SWEPT_FACE",FACE,{"disambiguationData":[OSD([sQuery(id+"F3.wireOp",EDGE,"E17.bottom")])]}),makeQuery(id+"F4.opExtrude","SWEPT_FACE",FACE,{"disambiguationData":[OSD([sQuery(id+"F3.wireOp",EDGE,"E18.bottom")])]})]}),makeQuery(id+"F6.opExtrude","SWEPT_FACE",FACE,{"disambiguationData":[OSD([sQuery(id+"F5.wireOp",EDGE,"E19.top")])]}),makeQuery(id+"F6.opExtrude","SWEPT_FACE",FACE,{"disambiguationData":[OSD([sQuery(id+"F5.wireOp",EDGE,"E20.top")])]}),makeQuery(id+"F6.opExtrude","SWEPT_FACE",FACE,{"disambiguationData":[OSD([sQuery(id+"F5.wireOp",EDGE,"E21.top")])]}),makeQuery(id+"F6.opExtrude","SWEPT_FACE",FACE,{"disambiguationData":[OSD([sQuery(id+"F5.wireOp",EDGE,"E22.top")])]})]});
            var sketch = newSketch(context, id + "F15", { "sketchPlane" : qUnion([Q0])});
            skCircle(sketch, "E124", {"center": v(0, 28.35) * mm, "radius": 1.6 * mm});
            skCircle(sketch, "E125", {"center": v(0, 28.35) * mm, "radius": 5.6 * mm});
            skSolve(sketch);
        }
        {
            var Q0;
            Q0 = qSketchRegion(id + "F15", true);
            extrude(context, id + "F16", {"entities" : qUnion([Q0]), "operationType" : NewBodyOperationType.ADD, "oppositeDirection" : true, "depth" : 12.2 * mm + 6 * mm});
        }
        {
            var Q0;
            Q0=makeQuery(id+"F15.imprint","IMPRINT",FACE,{"disambiguationData":[TD([[makeQuery(id+"F15.imprint","IMPRINT",EDGE,{"derivedFrom":sQuery(id+"F15.wireOp",EDGE,"E124")}),1.0]])]});
            extrude(context, id + "F17", {"entities" : qUnion([Q0]), "operationType" : NewBodyOperationType.REMOVE, "oppositeDirection" : true, "depth" : 25.4 * mm});
        }
        {
            var Q0;
            Q0=makeQuery(id+"F16.boolean.opBoolean","INTERSECT",EDGE,{"derivedFrom":[makeQuery(id+"F6.boolean.opBoolean","MERGE",FACE,{"derivedFrom":[makeQuery(id+"F4.boolean.opBoolean","MERGE",FACE,{"derivedFrom":[makeQuery(id+"F1.opExtrude","CAP_FACE",FACE,{"disambiguationData":[OSD([sQuery(id+"F0.wireOp",EDGE,"E0.bottom"),sQuery(id+"F0.wireOp",EDGE,"E0.top"),sQuery(id+"F0.wireOp",EDGE,"E0.left"),sQuery(id+"F0.wireOp",EDGE,"E0.right"),sQuery(id+"F0.wireOp",EDGE,"E2.top"),sQuery(id+"F0.wireOp",EDGE,"E2.left"),sQuery(id+"F0.wireOp",EDGE,"E2.right"),sQuery(id+"F0.wireOp",EDGE,"E4.bottom"),sQuery(id+"F0.wireOp",EDGE,"E4.top"),sQuery(id+"F0.wireOp",EDGE,"E4.left"),sQuery(id+"F0.wireOp",EDGE,"E4.right"),sQuery(id+"F0.wireOp",EDGE,"E8.MirrorCS"),sQuery(id+"F0.wireOp",EDGE,"E9.MirrorCS"),sQuery(id+"F0.wireOp",EDGE,"E10.MirrorCS"),sQuery(id+"F0.wireOp",EDGE,"E11.MirrorCS")])],"isStart":true}),makeQuery(id+"F4.opExtrude","SWEPT_FACE",FACE,{"disambiguationData":[OSD([sQuery(id+"F3.wireOp",EDGE,"E12.top")])]}),makeQuery(id+"F4.opExtrude","SWEPT_FACE",FACE,{"disambiguationData":[OSD([sQuery(id+"F3.wireOp",EDGE,"E13.MirrorCS")])]}),makeQuery(id+"F4.opExtrude","SWEPT_FACE",FACE,{"disambiguationData":[OSD([sQuery(id+"F3.wireOp",EDGE,"E17.top")])]}),makeQuery(id+"F4.opExtrude","SWEPT_FACE",FACE,{"disambiguationData":[OSD([sQuery(id+"F3.wireOp",EDGE,"E18.top")])]})]}),makeQuery(id+"F6.opExtrude","SWEPT_FACE",FACE,{"disambiguationData":[OSD([sQuery(id+"F5.wireOp",EDGE,"E19.bottom")])]}),makeQuery(id+"F6.opExtrude","SWEPT_FACE",FACE,{"disambiguationData":[OSD([sQuery(id+"F5.wireOp",EDGE,"E20.bottom")])]}),makeQuery(id+"F6.opExtrude","SWEPT_FACE",FACE,{"disambiguationData":[OSD([sQuery(id+"F5.wireOp",EDGE,"E21.bottom")])]}),makeQuery(id+"F6.opExtrude","SWEPT_FACE",FACE,{"disambiguationData":[OSD([sQuery(id+"F5.wireOp",EDGE,"E22.bottom")])]})]}),makeQuery(id+"F16.opExtrude","SWEPT_FACE",FACE,{"disambiguationData":[OSD([sQuery(id+"F15.wireOp",EDGE,"E125")])]})]});
            fillet(context, id + "F18", {"entities" : qUnion([Q0]), "radius" : 5.08 * mm, "tangentPropagation" : true, "allowEdgeOverflow" : false});
        }
    });
